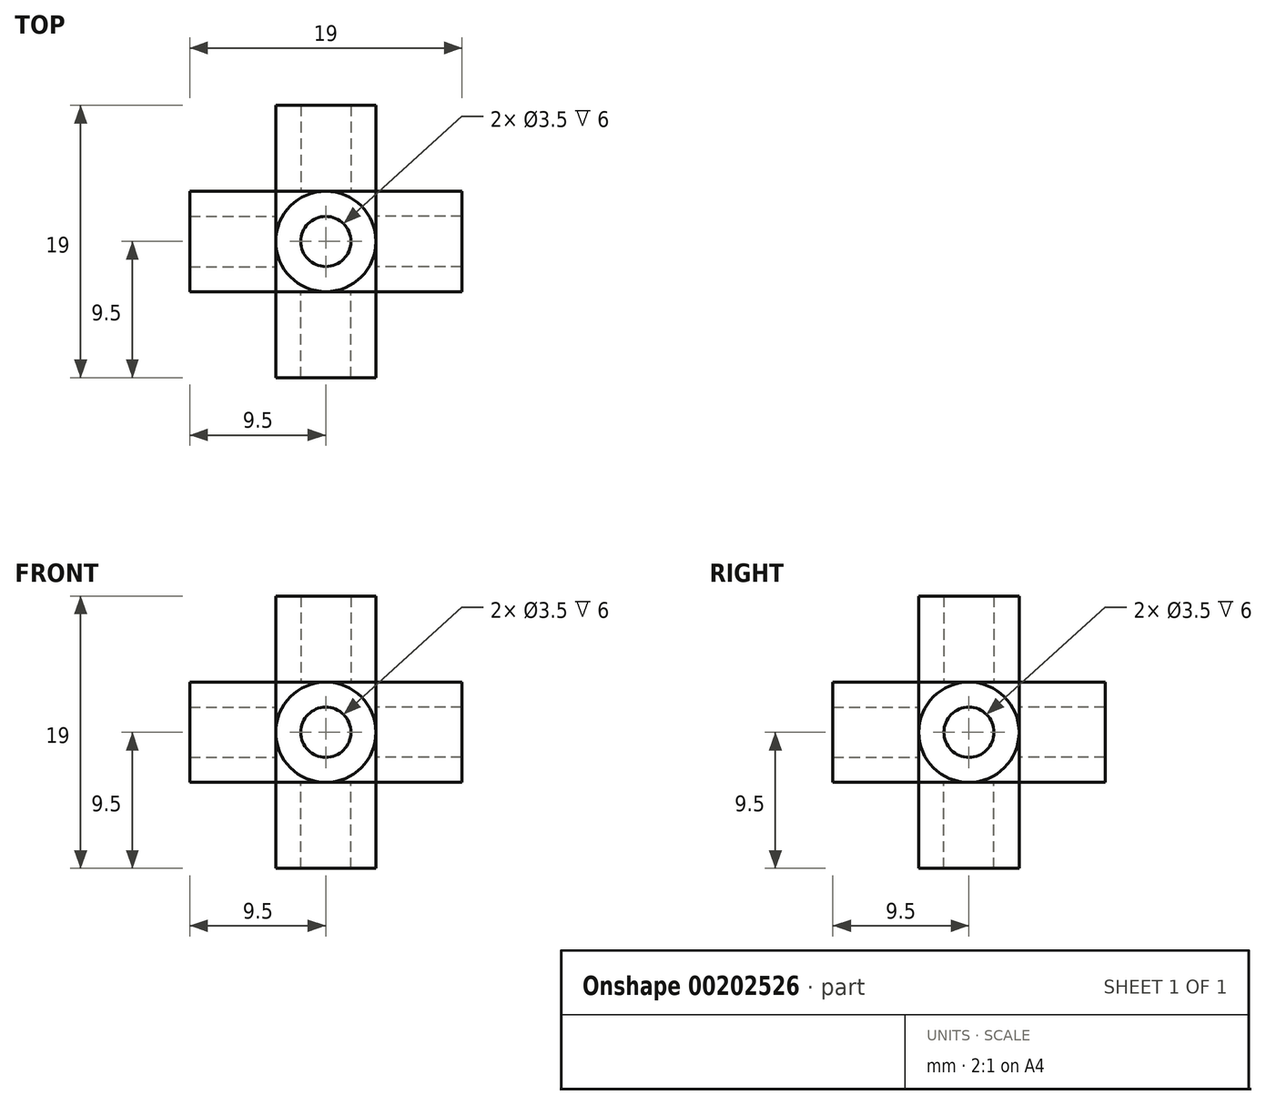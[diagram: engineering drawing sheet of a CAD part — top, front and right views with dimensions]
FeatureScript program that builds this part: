
annotation { "Feature Type Name" : "Feature", "Feature Type Description" : "" }
export const myFeature = defineFeature(function(context is Context, id is Id, definition is map)
    precondition{}
    {
        {
            var Q0;
            Q0=qCreatedBy(makeId("Front.planeOp"),FACE);
            var sketch = newSketch(context, id + "F0", { "sketchPlane" : qUnion([Q0])});
            skLineSegment(sketch, "E0.bottom", {"start": v(-3.5, 3.5) * mm, "end": v(3.5, 3.5) * mm});
            skLineSegment(sketch, "E0.top", {"start": v(-3.5, -3.5) * mm, "end": v(3.5, -3.5) * mm});
            skLineSegment(sketch, "E0.left", {"start": v(-3.5, 3.5) * mm, "end": v(-3.5, -3.5) * mm});
            skLineSegment(sketch, "E0.right", {"start": v(3.5, 3.5) * mm, "end": v(3.5, -3.5) * mm});
            skPoint(sketch, "E0.middle", {"position": v(0, 0) * mm});
            skSolve(sketch);
        }
        {
            var Q0;
            Q0 = qSketchRegion(id + "F0", true);
            extrude(context, id + "F1", {"entities" : qUnion([Q0]), "depth" : 7 * mm, "symmetric" : true});
        }
        {
            var Q0;
            Q0=makeQuery(id+"F1.opExtrude","CAP_FACE",FACE,{"disambiguationData":[OSD([sQuery(id+"F0.wireOp",EDGE,"E0.bottom"),sQuery(id+"F0.wireOp",EDGE,"E0.top"),sQuery(id+"F0.wireOp",EDGE,"E0.left"),sQuery(id+"F0.wireOp",EDGE,"E0.right")])],"isStart":false});
            var sketch = newSketch(context, id + "F2", { "sketchPlane" : qUnion([Q0])});
            skCircle(sketch, "E1", {"center": v(0, 0) * mm, "radius": 3.5 * mm});
            skCircle(sketch, "E2", {"center": v(0, 0) * mm, "radius": 1.75 * mm});
            skSolve(sketch);
        }
        {
            var Q0;
            Q0 = qSketchRegion(id + "F2", true);
            extrude(context, id + "F3", {"entities" : qUnion([Q0]), "operationType" : NewBodyOperationType.ADD, "depth" : 6 * mm});
        }
        {
            var Q0;
            Q0=makeQuery(id+"F1.opExtrude","SWEPT_FACE",FACE,{"disambiguationData":[OSD([sQuery(id+"F0.wireOp",EDGE,"E0.top")])]});
            var sketch = newSketch(context, id + "F4", { "sketchPlane" : qUnion([Q0])});
            skCircle(sketch, "E3", {"center": v(0, 0) * mm, "radius": 3.5 * mm});
            skCircle(sketch, "E4", {"center": v(0, 0) * mm, "radius": 1.75 * mm});
            skSolve(sketch);
        }
        {
            var Q0;
            Q0 = qSketchRegion(id + "F4", true);
            extrude(context, id + "F5", {"entities" : qUnion([Q0]), "operationType" : NewBodyOperationType.ADD, "depth" : 6 * mm});
        }
        {
            var Q0;
            Q0=makeQuery(id+"F1.opExtrude","CAP_FACE",FACE,{"disambiguationData":[OSD([sQuery(id+"F0.wireOp",EDGE,"E0.bottom"),sQuery(id+"F0.wireOp",EDGE,"E0.top"),sQuery(id+"F0.wireOp",EDGE,"E0.left"),sQuery(id+"F0.wireOp",EDGE,"E0.right")])],"isStart":true});
            var sketch = newSketch(context, id + "F6", { "sketchPlane" : qUnion([Q0])});
            skCircle(sketch, "E5", {"center": v(0, 0) * mm, "radius": 3.5 * mm});
            skCircle(sketch, "E6", {"center": v(0, 0) * mm, "radius": 1.75 * mm});
            skSolve(sketch);
        }
        {
            var Q0;
            Q0 = qSketchRegion(id + "F6", true);
            extrude(context, id + "F7", {"entities" : qUnion([Q0]), "operationType" : NewBodyOperationType.ADD, "depth" : 6 * mm});
        }
        {
            var Q0;
            Q0=makeQuery(id+"F1.opExtrude","SWEPT_FACE",FACE,{"disambiguationData":[OSD([sQuery(id+"F0.wireOp",EDGE,"E0.bottom")])]});
            var sketch = newSketch(context, id + "F8", { "sketchPlane" : qUnion([Q0])});
            skCircle(sketch, "E7", {"center": v(0, 0) * mm, "radius": 3.5 * mm});
            skCircle(sketch, "E8", {"center": v(0, 0) * mm, "radius": 1.75 * mm});
            skSolve(sketch);
        }
        {
            var Q0;
            Q0 = qSketchRegion(id + "F8", true);
            extrude(context, id + "F9", {"entities" : qUnion([Q0]), "operationType" : NewBodyOperationType.ADD, "depth" : 6 * mm});
        }
        {
            var Q0;
            Q0=makeQuery(id+"F1.opExtrude","SWEPT_FACE",FACE,{"disambiguationData":[OSD([sQuery(id+"F0.wireOp",EDGE,"E0.left")])]});
            var sketch = newSketch(context, id + "F10", { "sketchPlane" : qUnion([Q0])});
            skCircle(sketch, "E9", {"center": v(0, 0) * mm, "radius": 3.5 * mm});
            skCircle(sketch, "E10", {"center": v(0, 0) * mm, "radius": 1.75 * mm});
            skSolve(sketch);
        }
        {
            var Q0;
            Q0 = qSketchRegion(id + "F10", true);
            extrude(context, id + "F11", {"entities" : qUnion([Q0]), "operationType" : NewBodyOperationType.ADD, "depth" : 6 * mm});
        }
        {
            var Q0;
            Q0=makeQuery(id+"F1.opExtrude","SWEPT_FACE",FACE,{"disambiguationData":[OSD([sQuery(id+"F0.wireOp",EDGE,"E0.right")])]});
            var sketch = newSketch(context, id + "F12", { "sketchPlane" : qUnion([Q0])});
            skCircle(sketch, "E11", {"center": v(0, 0) * mm, "radius": 3.5 * mm});
            skCircle(sketch, "E12", {"center": v(0, 0) * mm, "radius": 1.75 * mm});
            skSolve(sketch);
        }
        {
            var Q0;
            Q0 = qSketchRegion(id + "F12", true);
            extrude(context, id + "F13", {"entities" : qUnion([Q0]), "operationType" : NewBodyOperationType.ADD, "depth" : 6 * mm});
        }
    });
